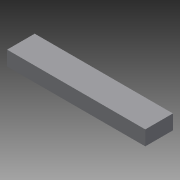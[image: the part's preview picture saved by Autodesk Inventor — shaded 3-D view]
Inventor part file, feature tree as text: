
AUTODESK INVENTOR PART (.ipt)
format: ipt  version: 2014 SP1 (Build 180222100, 222)  size: 67,584 bytes
history: native  units: in
note: dims shown in document units (in); Inventor stores cm internally (conversion verified against a paired STEP export)
features: extrude x1, sketch x1
ambient origin geometry x8: Origin, YZ Plane, XZ Plane, XY Plane, X Axis, Y Axis, Z Axis, Center Point
bodies: Solid1 (feature_tree)
feature tree (2):
  extrude  "Extrusion1"  Depth=0.53in
  sketch  "Sketch1"  dims[d0=1.0in d1=0.53in d2=5.0in d3=0.0in]
